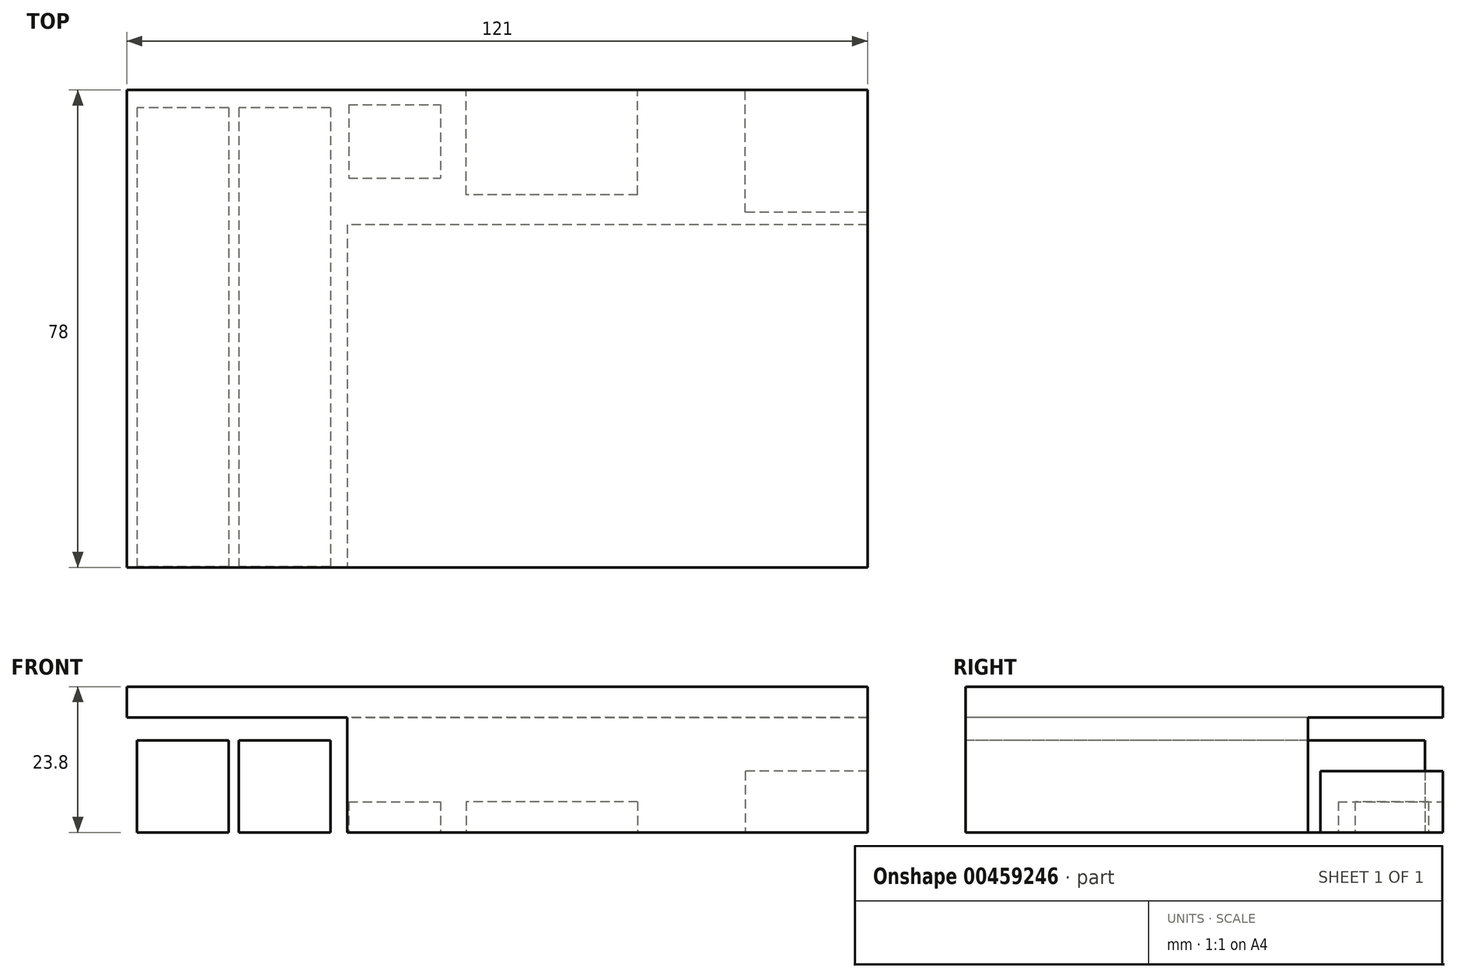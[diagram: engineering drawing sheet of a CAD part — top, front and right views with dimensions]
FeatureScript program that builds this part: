
annotation { "Feature Type Name" : "Feature", "Feature Type Description" : "" }
export const myFeature = defineFeature(function(context is Context, id is Id, definition is map)
    precondition{}
    {
        {
            var Q0;
            Q0=qCreatedBy(makeId("Top.planeOp"),FACE);
            var sketch = newSketch(context, id + "F0", { "sketchPlane" : qUnion([Q0])});
            skLineSegment(sketch, "E0.bottom", {"start": v(42.5, 28) * mm, "end": v(-42.5, 28) * mm});
            skLineSegment(sketch, "E0.top", {"start": v(42.5, -28) * mm, "end": v(-42.5, -28) * mm});
            skLineSegment(sketch, "E0.left", {"start": v(42.5, 28) * mm, "end": v(42.5, -28) * mm});
            skLineSegment(sketch, "E0.right", {"start": v(-42.5, 28) * mm, "end": v(-42.5, -28) * mm});
            skPoint(sketch, "E0.middle", {"position": v(0, 0) * mm});
            skSolve(sketch);
        }
        {
            var Q0;
            Q0 = qSketchRegion(id + "F0", true);
            extrude(context, id + "F1", {"entities" : qUnion([Q0]), "depth" : 18.8 * mm});
        }
        {
            var Q0;
            Q0=makeQuery(id+"F1.opExtrude","CAP_FACE",FACE,{"disambiguationData":[OSD([sQuery(id+"F0.wireOp",EDGE,"E0.bottom"),sQuery(id+"F0.wireOp",EDGE,"E0.top"),sQuery(id+"F0.wireOp",EDGE,"E0.left"),sQuery(id+"F0.wireOp",EDGE,"E0.right")])],"isStart":false});
            var sketch = newSketch(context, id + "F2", { "sketchPlane" : qUnion([Q0])});
            skLineSegment(sketch, "E1.bottom", {"start": v(-78.5, 50) * mm, "end": v(42.5, 50) * mm});
            skLineSegment(sketch, "E1.top", {"start": v(-78.5, -28) * mm, "end": v(42.5, -28) * mm});
            skLineSegment(sketch, "E1.left", {"start": v(-78.5, 50) * mm, "end": v(-78.5, -28) * mm});
            skLineSegment(sketch, "E1.right", {"start": v(42.5, 50) * mm, "end": v(42.5, -28) * mm});
            skPoint(sketch, "E2", {"position": v(42.5, 50) * mm});
            skSolve(sketch);
        }
        {
            var Q0;
            {var subQ4=makeQuery(id+"F1.opExtrude","CAP_EDGE",EDGE,{"disambiguationData":[OSD([sQuery(id+"F0.wireOp",EDGE,"E0.bottom")])],"isStart":false});Q0=makeQuery(id+"F2.imprint","IMPRINT",FACE,{"disambiguationData":[TD([[makeQuery(id+"F2.imprint","IMPRINT",EDGE,{"derivedFrom":subQ4}),1.0]])]});}
            var Q1;
            {var subQ2=sQuery(id+"F2.wireOp",EDGE,"E1.bottom");Q1=makeQuery(id+"F2.imprint","IMPRINT",FACE,{"disambiguationData":[TD([[makeQuery(id+"F2.imprint","IMPRINT",EDGE,{"derivedFrom":subQ2}),-1.0]])]});}
            extrude(context, id + "F3", {"entities" : qUnion([Q0, Q1]), "operationType" : NewBodyOperationType.ADD, "depth" : 5 * mm});
        }
        {
            var Q0;
            Q0=qCreatedBy(makeId("Top.planeOp"),FACE);
            var sketch = newSketch(context, id + "F4", { "sketchPlane" : qUnion([Q0])});
            skLineSegment(sketch, "E3.bottom", {"start": v(-61.89, 47.09) * mm, "end": v(-76.89, 47.09) * mm});
            skLineSegment(sketch, "E3.top", {"start": v(-61.89, -27.91) * mm, "end": v(-76.89, -27.91) * mm});
            skLineSegment(sketch, "E3.left", {"start": v(-61.89, 47.09) * mm, "end": v(-61.89, -27.91) * mm});
            skLineSegment(sketch, "E3.right", {"start": v(-76.89, 47.09) * mm, "end": v(-76.89, -27.91) * mm});
            skLineSegment(sketch, "E4.bottom", {"start": v(-45.23, 47.09) * mm, "end": v(-60.23, 47.09) * mm});
            skLineSegment(sketch, "E4.top", {"start": v(-45.23, -27.91) * mm, "end": v(-60.23, -27.91) * mm});
            skLineSegment(sketch, "E4.left", {"start": v(-45.23, 47.09) * mm, "end": v(-45.23, -27.91) * mm});
            skLineSegment(sketch, "E4.right", {"start": v(-60.23, 47.09) * mm, "end": v(-60.23, -27.91) * mm});
            skSolve(sketch);
        }
        {
            var Q0;
            Q0=makeQuery(id+"F4.imprint","IMPRINT",FACE,{"disambiguationData":[TD([[makeQuery(id+"F4.imprint","IMPRINT",EDGE,{"derivedFrom":sQuery(id+"F4.wireOp",EDGE,"E3.bottom")}),1.0]])]});
            var Q1;
            Q1=makeQuery(id+"F4.imprint","IMPRINT",FACE,{"disambiguationData":[TD([[makeQuery(id+"F4.imprint","IMPRINT",EDGE,{"derivedFrom":sQuery(id+"F4.wireOp",EDGE,"E4.bottom")}),1.0]])]});
            extrude(context, id + "F5", {"entities" : qUnion([Q0, Q1]), "depth" : 15 * mm});
        }
        {
            var Q0;
            Q0=qCreatedBy(makeId("Top.planeOp"),FACE);
            var sketch = newSketch(context, id + "F6", { "sketchPlane" : qUnion([Q0])});
            skLineSegment(sketch, "E5.bottom", {"start": v(-69.49, 12.15) * mm, "end": v(-51.49, 12.15) * mm});
            skLineSegment(sketch, "E5.top", {"start": v(-69.49, -21.85) * mm, "end": v(-51.49, -21.85) * mm});
            skLineSegment(sketch, "E5.left", {"start": v(-69.49, 12.15) * mm, "end": v(-69.49, -21.85) * mm});
            skLineSegment(sketch, "E5.right", {"start": v(-51.49, 12.15) * mm, "end": v(-51.49, -21.85) * mm});
            skSolve(sketch);
        }
        {
            var Q0;
            Q0=qCreatedBy(makeId("Top.planeOp"),FACE);
            var sketch = newSketch(context, id + "F7", { "sketchPlane" : qUnion([Q0])});
            skLineSegment(sketch, "E6.bottom", {"start": v(4.95, 32.9) * mm, "end": v(-23.05, 32.9) * mm});
            skLineSegment(sketch, "E6.top", {"start": v(4.95, 49.9) * mm, "end": v(-23.05, 49.9) * mm});
            skLineSegment(sketch, "E6.left", {"start": v(4.95, 32.9) * mm, "end": v(4.95, 49.9) * mm});
            skLineSegment(sketch, "E6.right", {"start": v(-23.05, 32.9) * mm, "end": v(-23.05, 49.9) * mm});
            skSolve(sketch);
        }
        {
            var Q0;
            Q0 = qSketchRegion(id + "F7", true);
            extrude(context, id + "F8", {"entities" : qUnion([Q0]), "depth" : 5 * mm});
        }
        {
            var Q0;
            Q0=qCreatedBy(makeId("Top.planeOp"),FACE);
            var sketch = newSketch(context, id + "F9", { "sketchPlane" : qUnion([Q0])});
            skLineSegment(sketch, "E7.bottom", {"start": v(-42.26, 47.63) * mm, "end": v(-27.26, 47.63) * mm});
            skLineSegment(sketch, "E7.top", {"start": v(-42.26, 35.63) * mm, "end": v(-27.26, 35.63) * mm});
            skLineSegment(sketch, "E7.left", {"start": v(-42.26, 47.63) * mm, "end": v(-42.26, 35.63) * mm});
            skLineSegment(sketch, "E7.right", {"start": v(-27.26, 47.63) * mm, "end": v(-27.26, 35.63) * mm});
            skSolve(sketch);
        }
        {
            var Q0;
            Q0 = qSketchRegion(id + "F9", true);
            extrude(context, id + "F10", {"entities" : qUnion([Q0]), "depth" : 5 * mm});
        }
        {
            var Q0;
            Q0=qCreatedBy(makeId("Top.planeOp"),FACE);
            var sketch = newSketch(context, id + "F11", { "sketchPlane" : qUnion([Q0])});
            skLineSegment(sketch, "E8.bottom", {"start": v(42.5, 30) * mm, "end": v(22.5, 30) * mm});
            skLineSegment(sketch, "E8.top", {"start": v(42.5, 50) * mm, "end": v(22.5, 50) * mm});
            skLineSegment(sketch, "E8.left", {"start": v(42.5, 30) * mm, "end": v(42.5, 50) * mm});
            skLineSegment(sketch, "E8.right", {"start": v(22.5, 30) * mm, "end": v(22.5, 50) * mm});
            skSolve(sketch);
        }
        {
            var Q0;
            Q0 = qSketchRegion(id + "F11", true);
            extrude(context, id + "F12", {"entities" : qUnion([Q0]), "depth" : 10 * mm});
        }
    });
